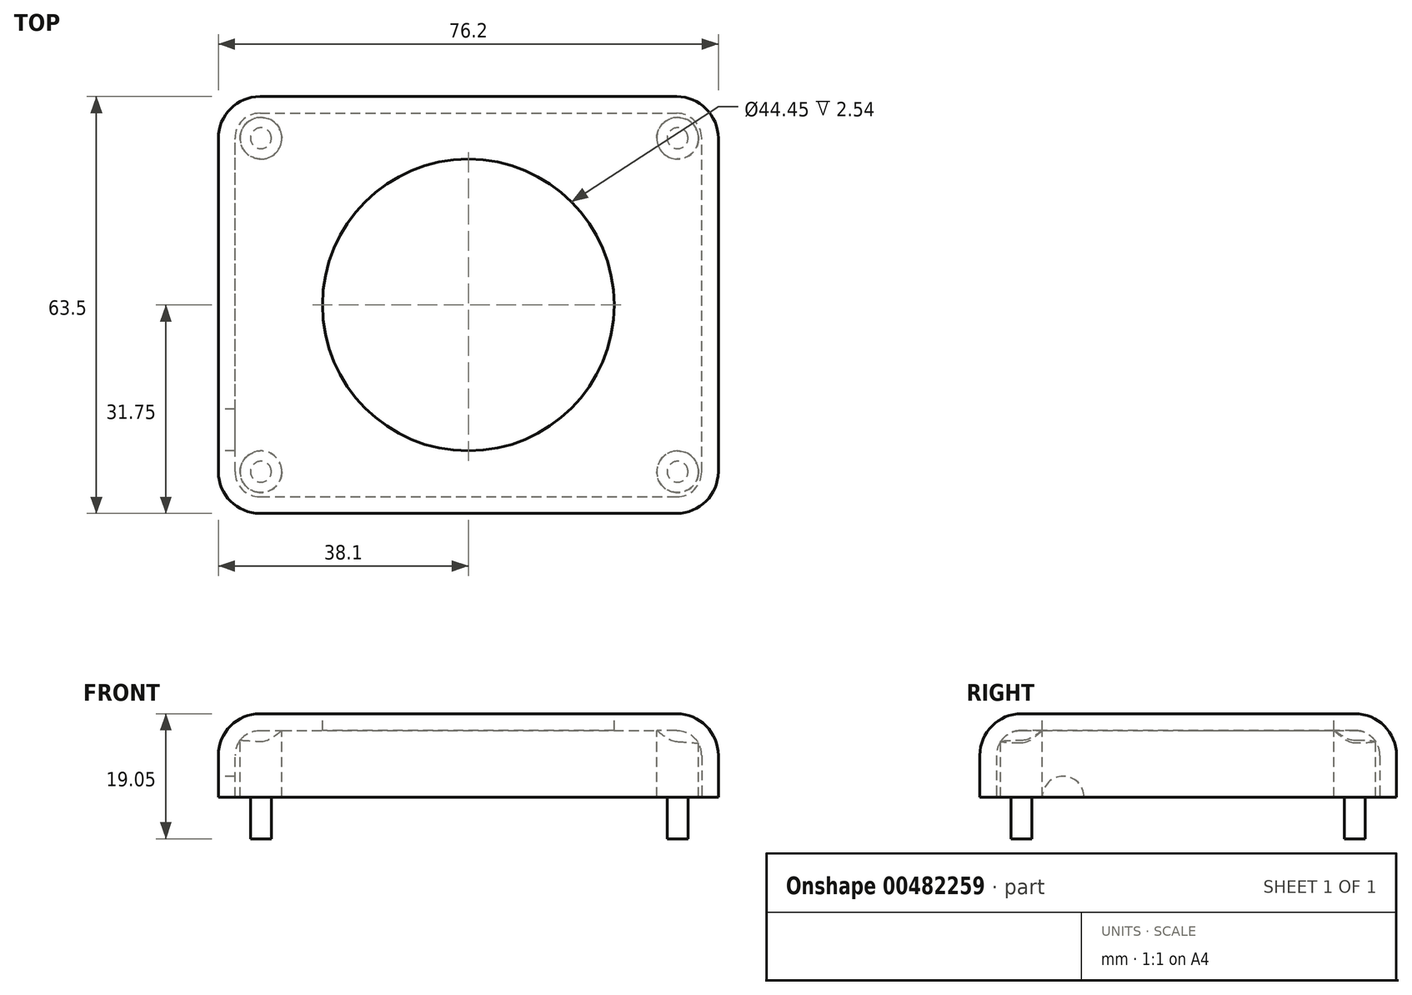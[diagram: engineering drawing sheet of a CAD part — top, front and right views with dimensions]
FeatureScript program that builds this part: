
annotation { "Feature Type Name" : "Feature", "Feature Type Description" : "" }
export const myFeature = defineFeature(function(context is Context, id is Id, definition is map)
    precondition{}
    {
        {
            var Q0;
            Q0=qCreatedBy(makeId("Top.planeOp"),FACE);
            var sketch = newSketch(context, id + "F0", { "sketchPlane" : qUnion([Q0])});
            skLineSegment(sketch, "E0.bottom", {"start": v(31.75, -31.75) * mm, "end": v(-31.75, -31.75) * mm});
            skLineSegment(sketch, "E0.top", {"start": v(31.75, 31.75) * mm, "end": v(-31.75, 31.75) * mm});
            skLineSegment(sketch, "E0.left", {"start": v(38.1, -25.4) * mm, "end": v(38.1, 25.4) * mm});
            skLineSegment(sketch, "E0.right", {"start": v(-38.1, -25.4) * mm, "end": v(-38.1, 25.4) * mm});
            skPoint(sketch, "E0.middle", {"position": v(0, 0) * mm});
            skPoint(sketch, "E1.visualSharp", {"position": v(-38.1, 31.75) * mm});
            skArc(sketch, "E1.filletArc", {"start": v(-31.75, 31.75) * mm, "mid": v(-36.24, 29.9) * mm, "end": v(-38.1, 25.4) * mm});
            skPoint(sketch, "E2.visualSharp", {"position": v(38.1, 31.75) * mm});
            skArc(sketch, "E2.filletArc", {"start": v(38.1, 25.4) * mm, "mid": v(36.24, 29.9) * mm, "end": v(31.75, 31.75) * mm});
            skPoint(sketch, "E3.visualSharp", {"position": v(38.1, -31.75) * mm});
            skArc(sketch, "E3.filletArc", {"start": v(31.75, -31.75) * mm, "mid": v(36.24, -29.9) * mm, "end": v(38.1, -25.4) * mm});
            skPoint(sketch, "E4.visualSharp", {"position": v(-38.1, -31.75) * mm});
            skArc(sketch, "E4.filletArc", {"start": v(-38.1, -25.4) * mm, "mid": v(-36.24, -29.9) * mm, "end": v(-31.75, -31.75) * mm});
            skSolve(sketch);
        }
        {
            var Q0;
            Q0 = qSketchRegion(id + "F0", true);
            extrude(context, id + "F1", {"entities" : qUnion([Q0]), "depth" : 12.7 * mm});
        }
        {
            var Q0;
            Q0=makeQuery(id+"F1.opExtrude","CAP_FACE",FACE,{"disambiguationData":[OSD([sQuery(id+"F0.wireOp",EDGE,"E0.bottom"),sQuery(id+"F0.wireOp",EDGE,"E0.top"),sQuery(id+"F0.wireOp",EDGE,"E0.left"),sQuery(id+"F0.wireOp",EDGE,"E0.right")])],"isStart":false});
            fillet(context, id + "F2", {"entities" : qUnion([Q0]), "radius" : 6.35 * mm, "tangentPropagation" : true, "allowEdgeOverflow" : false});
        }
        {
            var Q0;
            Q0=makeQuery(id+"F1.opExtrude","CAP_FACE",FACE,{"disambiguationData":[OSD([sQuery(id+"F0.wireOp",EDGE,"E0.bottom"),sQuery(id+"F0.wireOp",EDGE,"E0.top"),sQuery(id+"F0.wireOp",EDGE,"E0.left"),sQuery(id+"F0.wireOp",EDGE,"E0.right"),sQuery(id+"F0.wireOp",EDGE,"E1.filletArc"),sQuery(id+"F0.wireOp",EDGE,"E2.filletArc"),sQuery(id+"F0.wireOp",EDGE,"E3.filletArc"),sQuery(id+"F0.wireOp",EDGE,"E4.filletArc")])],"isStart":true});
            shell(context, id + "F3", {"entities" : qUnion([Q0]), "thickness" : 2.54 * mm});
        }
        {
            var Q0;
            Q0=makeQuery(id+"F1.opExtrude","SWEPT_FACE",FACE,{"disambiguationData":[OSD([sQuery(id+"F0.wireOp",EDGE,"E0.right")])]});
            var sketch = newSketch(context, id + "F4", { "sketchPlane" : qUnion([Q0])});
            skCircle(sketch, "E5", {"center": v(19.05, 0) * mm, "radius": 3.18 * mm});
            skSolve(sketch);
        }
        {
            var Q0;
            Q0 = qSketchRegion(id + "F4", true);
            var Q1;
            {var subQ0=sQuery(id+"F0.wireOp",EDGE,"E0.right");Q1=makeQuery(id+"F3.opShell","OFFSET_FACE",FACE,{"disambiguationData":[OSD([subQ0]),TDD([makeQuery(id+"F1.opExtrude","SWEPT_FACE",FACE,{"disambiguationData":[OSD([subQ0])]})])]});}
            extrude(context, id + "F5", {"entities" : qUnion([Q0]), "operationType" : NewBodyOperationType.REMOVE, "endBound" : BoundingType.UP_TO_SURFACE, "oppositeDirection" : true, "endBoundEntityFace" : qUnion([Q1]), "depth" : 25.4 * mm});
        }
        {
            var Q0;
            Q0=makeQuery(id+"F3.opShell","OFFSET_FACE",FACE,{"disambiguationData":[OSD([sQuery(id+"F0.wireOp",EDGE,"E0.bottom"),sQuery(id+"F0.wireOp",EDGE,"E0.top"),sQuery(id+"F0.wireOp",EDGE,"E0.left"),sQuery(id+"F0.wireOp",EDGE,"E0.right"),sQuery(id+"F0.wireOp",EDGE,"E1.filletArc"),sQuery(id+"F0.wireOp",EDGE,"E2.filletArc"),sQuery(id+"F0.wireOp",EDGE,"E3.filletArc"),sQuery(id+"F0.wireOp",EDGE,"E4.filletArc")])]});
            cPlane(context, id + "F6", {"entities" : qUnion([Q0]), "cplaneType" : CPlaneType.OFFSET, "offset" : 0 * mm, "width" : 152.4 * mm, "height" : 152.4 * mm});
        }
        {
            var Q0;
            Q0=qCreatedBy(id+"F6.planeOp",FACE);
            var sketch = newSketch(context, id + "F7", { "sketchPlane" : qUnion([Q0])});
            skCircle(sketch, "E6", {"center": v(-31.6, 25.4) * mm, "radius": 3.18 * mm});
            skCircle(sketch, "E7.0.1.0", {"center": v(-31.6, -25.4) * mm, "radius": 3.18 * mm});
            skCircle(sketch, "E7.1.0.0", {"center": v(31.9, 25.4) * mm, "radius": 3.18 * mm});
            skCircle(sketch, "E7.1.1.0", {"center": v(31.9, -25.4) * mm, "radius": 3.18 * mm});
            skLineSegment(sketch, "E7.direction1", {"start": v(-31.6, 25.4) * mm, "end": v(31.9, 25.4) * mm, "construction": true});
            skLineSegment(sketch, "E7.direction2", {"start": v(-31.6, 25.4) * mm, "end": v(-31.6, -25.4) * mm, "construction": true});
            skSolve(sketch);
        }
        {
            var Q0;
            Q0 = qSketchRegion(id + "F7", true);
            var Q1;
            Q1=makeQuery(id+"F1.opExtrude","CAP_FACE",FACE,{"disambiguationData":[OSD([sQuery(id+"F0.wireOp",EDGE,"E0.bottom"),sQuery(id+"F0.wireOp",EDGE,"E0.top"),sQuery(id+"F0.wireOp",EDGE,"E0.left"),sQuery(id+"F0.wireOp",EDGE,"E0.right"),sQuery(id+"F0.wireOp",EDGE,"E1.filletArc"),sQuery(id+"F0.wireOp",EDGE,"E2.filletArc"),sQuery(id+"F0.wireOp",EDGE,"E3.filletArc"),sQuery(id+"F0.wireOp",EDGE,"E4.filletArc")])],"isStart":true});
            extrude(context, id + "F8", {"entities" : qUnion([Q0]), "operationType" : NewBodyOperationType.ADD, "endBound" : BoundingType.UP_TO_SURFACE, "endBoundEntityFace" : qUnion([Q1]), "depth" : 12.7 * mm});
        }
        {
            var Q0;
            Q0=makeQuery(id+"F8.opExtrude","CAP_FACE",FACE,{"disambiguationData":[OSD([sQuery(id+"F7.wireOp",EDGE,"E6")])],"isStart":false});
            var sketch = newSketch(context, id + "F9", { "sketchPlane" : qUnion([Q0])});
            skCircle(sketch, "E8", {"center": v(-31.6, 25.4) * mm, "radius": 1.59 * mm});
            skCircle(sketch, "E9.0.1.0", {"center": v(-31.6, -25.4) * mm, "radius": 1.59 * mm});
            skCircle(sketch, "E9.1.0.0", {"center": v(31.9, 25.4) * mm, "radius": 1.59 * mm});
            skCircle(sketch, "E9.1.1.0", {"center": v(31.9, -25.4) * mm, "radius": 1.59 * mm});
            skLineSegment(sketch, "E9.direction1", {"start": v(-31.6, 25.4) * mm, "end": v(31.9, 25.4) * mm, "construction": true});
            skLineSegment(sketch, "E9.direction2", {"start": v(-31.6, 25.4) * mm, "end": v(-31.6, -25.4) * mm, "construction": true});
            skSolve(sketch);
        }
        {
            var Q0;
            Q0 = qSketchRegion(id + "F9", true);
            extrude(context, id + "F10", {"entities" : qUnion([Q0]), "operationType" : NewBodyOperationType.ADD, "depth" : 6.35 * mm});
        }
        {
            var Q0;
            Q0=makeQuery(id+"F1.opExtrude","CAP_FACE",FACE,{"disambiguationData":[OSD([sQuery(id+"F0.wireOp",EDGE,"E0.bottom"),sQuery(id+"F0.wireOp",EDGE,"E0.top"),sQuery(id+"F0.wireOp",EDGE,"E0.left"),sQuery(id+"F0.wireOp",EDGE,"E0.right"),sQuery(id+"F0.wireOp",EDGE,"E1.filletArc"),sQuery(id+"F0.wireOp",EDGE,"E2.filletArc"),sQuery(id+"F0.wireOp",EDGE,"E3.filletArc"),sQuery(id+"F0.wireOp",EDGE,"E4.filletArc")])],"isStart":false});
            var sketch = newSketch(context, id + "F11", { "sketchPlane" : qUnion([Q0])});
            skCircle(sketch, "E10", {"center": v(0, 0) * mm, "radius": 22.22 * mm});
            skSolve(sketch);
        }
        {
            var Q0;
            Q0 = qSketchRegion(id + "F11", true);
            var Q1;
            Q1=makeQuery(id+"F3.opShell","OFFSET_FACE",FACE,{"disambiguationData":[OSD([sQuery(id+"F0.wireOp",EDGE,"E0.bottom"),sQuery(id+"F0.wireOp",EDGE,"E0.top"),sQuery(id+"F0.wireOp",EDGE,"E0.left"),sQuery(id+"F0.wireOp",EDGE,"E0.right"),sQuery(id+"F0.wireOp",EDGE,"E1.filletArc"),sQuery(id+"F0.wireOp",EDGE,"E2.filletArc"),sQuery(id+"F0.wireOp",EDGE,"E3.filletArc"),sQuery(id+"F0.wireOp",EDGE,"E4.filletArc")])]});
            extrude(context, id + "F12", {"entities" : qUnion([Q0]), "operationType" : NewBodyOperationType.REMOVE, "endBound" : BoundingType.UP_TO_SURFACE, "oppositeDirection" : true, "endBoundEntityFace" : qUnion([Q1]), "depth" : 25.4 * mm});
        }
    });
